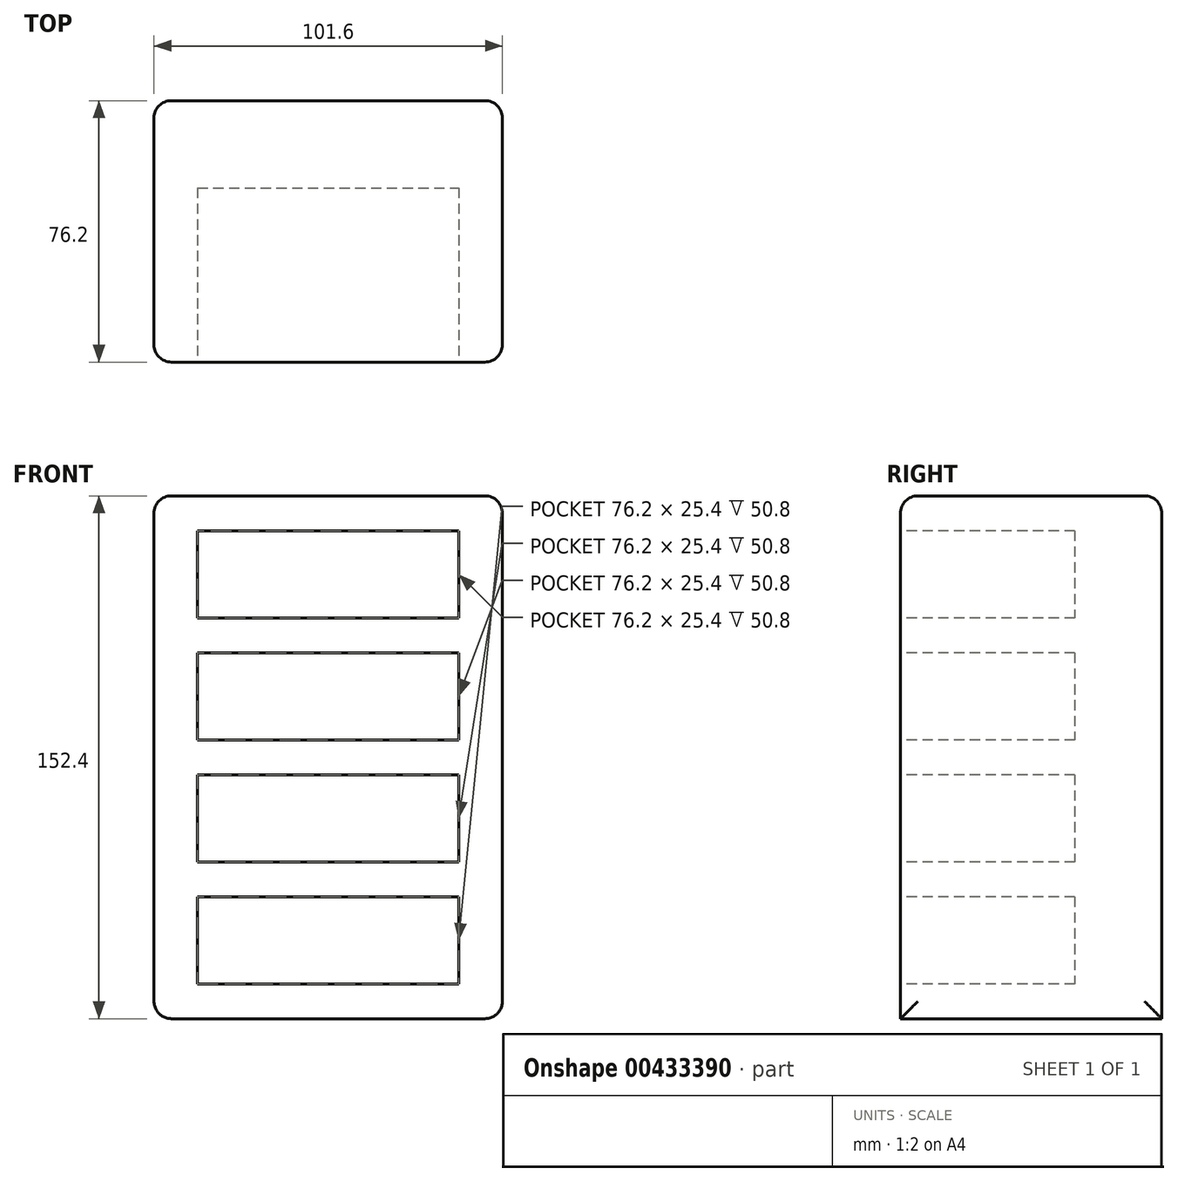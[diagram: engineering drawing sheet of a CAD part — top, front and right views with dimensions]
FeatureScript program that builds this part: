
annotation { "Feature Type Name" : "Feature", "Feature Type Description" : "" }
export const myFeature = defineFeature(function(context is Context, id is Id, definition is map)
    precondition{}
    {
        {
            var Q0;
            Q0=qCreatedBy(makeId("Top.planeOp"),FACE);
            var sketch = newSketch(context, id + "F0", { "sketchPlane" : qUnion([Q0])});
            skLineSegment(sketch, "E0.bottom", {"start": v(-50.75, 36.82) * mm, "end": v(50.85, 36.82) * mm});
            skLineSegment(sketch, "E0.top", {"start": v(-50.75, -39.38) * mm, "end": v(50.85, -39.38) * mm});
            skLineSegment(sketch, "E0.left", {"start": v(-50.75, 36.82) * mm, "end": v(-50.75, -39.38) * mm});
            skLineSegment(sketch, "E0.right", {"start": v(50.85, 36.82) * mm, "end": v(50.85, -39.38) * mm});
            skSolve(sketch);
        }
        {
            var Q0;
            Q0=makeQuery(id+"F0.imprint","IMPRINT",FACE,{"disambiguationData":[TD([[makeQuery(id+"F0.imprint","IMPRINT",EDGE,{"derivedFrom":sQuery(id+"F0.wireOp",EDGE,"E0.bottom")}),-1.0]])]});
            extrude(context, id + "F1", {"entities" : qUnion([Q0]), "depth" : 152.4 * mm});
        }
        {
            var Q0;
            Q0=makeQuery(id+"F1.opExtrude","SWEPT_FACE",FACE,{"disambiguationData":[OSD([sQuery(id+"F0.wireOp",EDGE,"E0.top")])]});
            var sketch = newSketch(context, id + "F2", { "sketchPlane" : qUnion([Q0])});
            skLineSegment(sketch, "E1.bottom", {"start": v(-38.05, 142.24) * mm, "end": v(38.15, 142.24) * mm});
            skLineSegment(sketch, "E1.top", {"start": v(-38.05, 116.84) * mm, "end": v(38.15, 116.84) * mm});
            skLineSegment(sketch, "E1.left", {"start": v(-38.05, 142.24) * mm, "end": v(-38.05, 116.84) * mm});
            skLineSegment(sketch, "E1.right", {"start": v(38.15, 142.24) * mm, "end": v(38.15, 116.84) * mm});
            skLineSegment(sketch, "E2.0.1.0", {"start": v(-38.05, 106.68) * mm, "end": v(38.15, 106.68) * mm});
            skLineSegment(sketch, "E2.0.1.1", {"start": v(-38.05, 106.68) * mm, "end": v(-38.05, 81.28) * mm});
            skLineSegment(sketch, "E2.0.1.2", {"start": v(-38.05, 81.28) * mm, "end": v(38.15, 81.28) * mm});
            skLineSegment(sketch, "E2.0.1.3", {"start": v(38.15, 106.68) * mm, "end": v(38.15, 81.28) * mm});
            skLineSegment(sketch, "E2.0.2.0", {"start": v(-38.05, 71.12) * mm, "end": v(38.15, 71.12) * mm});
            skLineSegment(sketch, "E2.0.2.1", {"start": v(-38.05, 71.12) * mm, "end": v(-38.05, 45.72) * mm});
            skLineSegment(sketch, "E2.0.2.2", {"start": v(-38.05, 45.72) * mm, "end": v(38.15, 45.72) * mm});
            skLineSegment(sketch, "E2.0.2.3", {"start": v(38.15, 71.12) * mm, "end": v(38.15, 45.72) * mm});
            skLineSegment(sketch, "E2.0.3.0", {"start": v(-38.05, 35.56) * mm, "end": v(38.15, 35.56) * mm});
            skLineSegment(sketch, "E2.0.3.1", {"start": v(-38.05, 35.56) * mm, "end": v(-38.05, 10.16) * mm});
            skLineSegment(sketch, "E2.0.3.2", {"start": v(-38.05, 10.16) * mm, "end": v(38.15, 10.16) * mm});
            skLineSegment(sketch, "E2.0.3.3", {"start": v(38.15, 35.56) * mm, "end": v(38.15, 10.16) * mm});
            skLineSegment(sketch, "E2.direction1", {"start": v(-38.05, 142.24) * mm, "end": v(-12.65, 142.24) * mm, "construction": true});
            skLineSegment(sketch, "E2.direction2", {"start": v(-38.05, 142.24) * mm, "end": v(-38.05, 106.68) * mm, "construction": true});
            skSolve(sketch);
        }
        {
            var Q0;
            Q0 = qSketchRegion(id + "F2", true);
            extrude(context, id + "F3", {"entities" : qUnion([Q0]), "operationType" : NewBodyOperationType.REMOVE, "oppositeDirection" : true, "depth" : 50.8 * mm});
        }
        {
            var Q0;
            Q0=makeQuery(id+"F1.opExtrude","CAP_FACE",FACE,{"disambiguationData":[OSD([sQuery(id+"F0.wireOp",EDGE,"E0.bottom"),sQuery(id+"F0.wireOp",EDGE,"E0.top"),sQuery(id+"F0.wireOp",EDGE,"E0.left"),sQuery(id+"F0.wireOp",EDGE,"E0.right")])],"isStart":false});
            var Q1;
            Q1=makeQuery(id+"F1.opExtrude","SWEPT_FACE",FACE,{"disambiguationData":[OSD([sQuery(id+"F0.wireOp",EDGE,"E0.right")])]});
            var Q2;
            Q2=makeQuery(id+"F1.opExtrude","SWEPT_FACE",FACE,{"disambiguationData":[OSD([sQuery(id+"F0.wireOp",EDGE,"E0.left")])]});
            fillet(context, id + "F4", {"entities" : qUnion([Q0, Q1, Q2]), "radius" : 5.08 * mm, "tangentPropagation" : true, "allowEdgeOverflow" : false});
        }
    });
